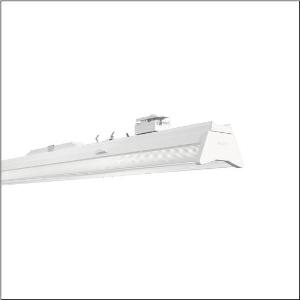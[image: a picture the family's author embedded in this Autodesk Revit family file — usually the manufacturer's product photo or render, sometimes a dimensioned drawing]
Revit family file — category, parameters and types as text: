
# Revit family: licross_r__21_performance_ho_52tm16mn4e5m_7be5
name_source: partatom
category: Lighting Fixtures
units: mm (PartAtom-declared; Revit-internal decimal feet)

## family parameters
Cut with Voids When Loaded = No
Host = Face
Light Source = No
Part Type = Normal
Room Calculation Point = No
Round Connector Dimension = Use Diameter
Shared = No

## types (1)
- --- (1 x LED, 14970 lm, 83.2 W, 4000K)
    Apparent Load = 83 VA
    CIE Flux Codes = 63 87 95 78 100
    Color Rendering = 80
    Color Temperature = 4000K
    Default Elevation = 1800 mm
    Description = Licross® 21 Performance HO, luminaire insert, of sheet steel, galvanised, coil coated, white, length: 1.500mm, width: 120mm, height: 123mm, LED rated luminous flux: 14.970lm, light colour: 840, control gear: ON/OFF Multilumen, with plug, 3-pole, with phase selection, mains connection: 220..240V, AC, 50/60Hz, rated input power: 83W, halogen-free wiring, primary light control with lens, of plastic, primary optical cover: cover, of PMMA, light emission: direct/indirect distribution, primary light characteristic: symmetric, protection rating (complete): IP40, insulation class (complete): insulation class I (protective earthing), certification: CE, ENEC, UKCA, protection symbol: D if used in an environment without relevant dust loads with corresponding accessories, impact resistance: IK06, permissible ambient temperature for indoor applications: -35..+35°C, corresponds to IFS (International Featured Standards) requirements for safety and quality in the food industry, reducing of maximum allowable ambient temperature of 5°C with ceiling mounting, LABS conformity tested according to VDMA 24364:2018-05, packaging unit: 1 piece
    Height = 114 mm
    Lamp = 1 x LED
    Lamp Light Flux = 14970 lm
    Lamp Power = 83.2 W
    Lamp count = 1
    Length = 1500 mm
    Luminous efficacy = 180 lm/W
    Manufacturer = Siteco
    ModVariant = No
    Model = 52TM16MN4E5M
    Mounting Place = Ceiling
    Mounting Type = Pendant
    Number of Poles = 1
    OnlyDefault = Yes
    Power Factor = 1
    Product Name = Licross® 21 Performance HO
    Product group = luminaire insert
    ProductGroupID = 901
    Protection Class = Protection class I
    Protection Degree = IP 40
    RLX_Detail_Level = 1
    RLX_Emergency_Light_Flux = 0 lm
    RLX_Emergency_Type = 0
    RLX_Emergency_Type_DB = No
    RlxData = <blob elided: 31793 chars, md5=1b5726b3>
    Socket = socket
    Standby Power = 0 W
    System Light Flux = 14970 lm
    System Power = 83 W
    Type Comments = factory setting: luminous flux: 100 % | (A | C | E) | 195 mA
    Type Image = l_1256138.jpg
    URL = http://relux.com
    VarID = @adj_039383
    Voltage = 0 V
    Weight = 0.00 kg
    Width = 120 mm

## geometry (parser evidence)
native form markers: Blend x4, Sweep x12
no freeform markers — native parametric forms only
